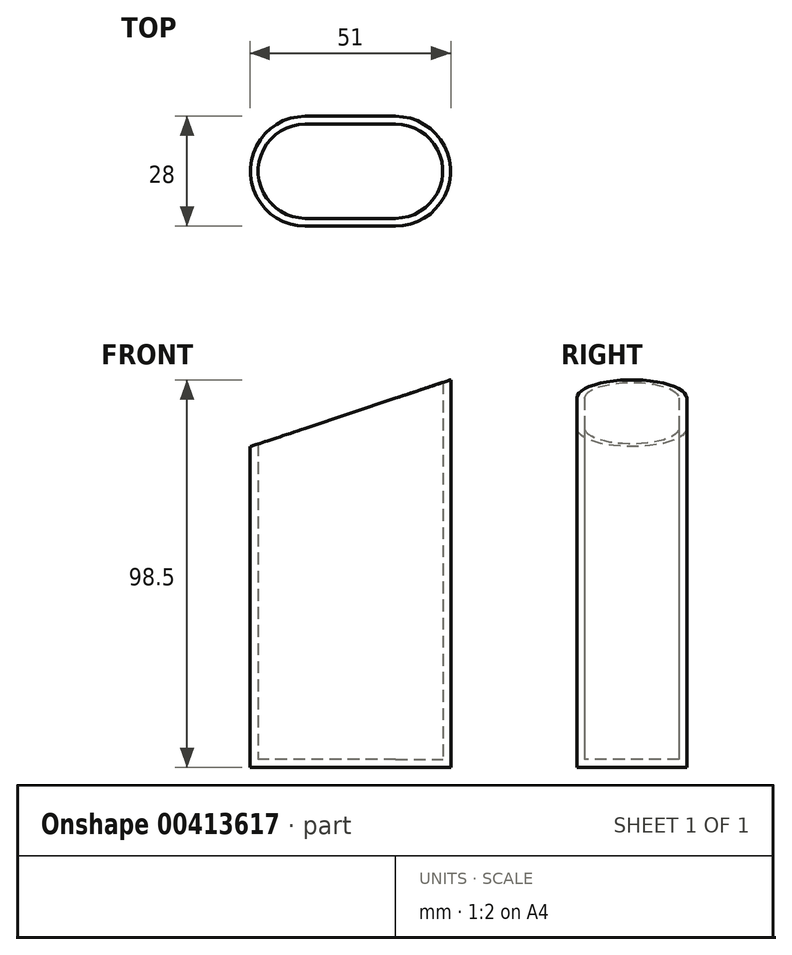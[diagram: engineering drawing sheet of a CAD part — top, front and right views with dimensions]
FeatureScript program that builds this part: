
annotation { "Feature Type Name" : "Feature", "Feature Type Description" : "" }
export const myFeature = defineFeature(function(context is Context, id is Id, definition is map)
    precondition{}
    {
        {
            var Q0;
            Q0=qCreatedBy(makeId("Top.planeOp"),FACE);
            var sketch = newSketch(context, id + "F0", { "sketchPlane" : qUnion([Q0])});
            skLineSegment(sketch, "E0.bottom", {"start": v(11.5, 12) * mm, "end": v(-11.5, 12) * mm});
            skLineSegment(sketch, "E0.top", {"start": v(11.5, -12) * mm, "end": v(-11.5, -12) * mm});
            skLineSegment(sketch, "E0.left", {"start": v(23.5, 0) * mm, "end": v(23.5, 0) * mm});
            skLineSegment(sketch, "E0.right", {"start": v(-23.5, 0) * mm, "end": v(-23.5, 0) * mm});
            skPoint(sketch, "E0.middle", {"position": v(0, 0) * mm});
            skPoint(sketch, "E1.visualSharp", {"position": v(23.5, 12) * mm});
            skArc(sketch, "E1.filletArc", {"start": v(23.5, 0) * mm, "mid": v(19.99, 8.49) * mm, "end": v(11.5, 12) * mm});
            skPoint(sketch, "E2.visualSharp", {"position": v(23.5, -12) * mm});
            skArc(sketch, "E2.filletArc", {"start": v(11.5, -12) * mm, "mid": v(19.99, -8.49) * mm, "end": v(23.5, 0) * mm});
            skPoint(sketch, "E3.visualSharp", {"position": v(-23.5, 12) * mm});
            skArc(sketch, "E3.filletArc", {"start": v(-11.5, 12) * mm, "mid": v(-19.99, 8.49) * mm, "end": v(-23.5, 0) * mm});
            skPoint(sketch, "E4.visualSharp", {"position": v(-23.5, -12) * mm});
            skArc(sketch, "E4.filletArc", {"start": v(-23.5, 0) * mm, "mid": v(-19.99, -8.49) * mm, "end": v(-11.5, -12) * mm});
            skArc(sketch, "E5.0", {"start": v(25.5, 0) * mm, "mid": v(21.4, 9.9) * mm, "end": v(11.5, 14) * mm});
            skArc(sketch, "E5.1", {"start": v(-11.5, 14) * mm, "mid": v(-21.4, -9.9) * mm, "end": v(2.5, 0) * mm});
            skArc(sketch, "E5.2", {"start": v(2.5, 0) * mm, "mid": v(-21.4, 9.9) * mm, "end": v(-11.5, -14) * mm});
            skLineSegment(sketch, "E5.3", {"start": v(11.5, 14) * mm, "end": v(-11.5, 14) * mm});
            skLineSegment(sketch, "E5.4", {"start": v(11.5, -14) * mm, "end": v(-11.5, -14) * mm});
            skArc(sketch, "E5.5", {"start": v(11.5, -14) * mm, "mid": v(21.4, -9.9) * mm, "end": v(25.5, 0) * mm});
            skPoint(sketch, "E6", {"position": v(2.5, 0) * mm});
            skPoint(sketch, "E7", {"position": v(25.5, 0) * mm});
            skSolve(sketch);
        }
        {
            var Q0;
            Q0=makeQuery(id+"F0.imprint","IMPRINT",FACE,{"disambiguationData":[TD([[makeQuery(id+"F0.imprint","IMPRINT",EDGE,{"derivedFrom":sQuery(id+"F0.wireOp",EDGE,"E0.bottom")}),1.0]])]});
            var Q1;
            Q1=makeQuery(id+"F0.imprint","IMPRINT",FACE,{"disambiguationData":[TD([[makeQuery(id+"F0.imprint","IMPRINT",EDGE,{"derivedFrom":sQuery(id+"F0.wireOp",EDGE,"E0.bottom")}),-1.0]])]});
            var Q2;
            {var subQ4=sQuery(id+"F0.wireOp",EDGE,"E3.filletArc");Q2=makeQuery(id+"F0.imprint","IMPRINT",FACE,{"disambiguationData":[TD([[makeQuery(id+"F0.imprint","IMPRINT",EDGE,{"derivedFrom":subQ4}),-1.0]])]});}
            extrude(context, id + "F1", {"entities" : qUnion([Q0, Q1, Q2]), "depth" : 2 * mm});
        }
        {
            var Q0;
            Q0 = qSketchRegion(id + "F0", true);
            extrude(context, id + "F2", {"entities" : qUnion([Q0]), "operationType" : NewBodyOperationType.ADD, "depth" : 100 * mm});
        }
        {
            var Q0;
            Q0=makeQuery(id+"F2.opExtrude","SWEPT_FACE",FACE,{"disambiguationData":[OSD([sQuery(id+"F0.wireOp",EDGE,"E5.3")])]});
            var sketch = newSketch(context, id + "F3", { "sketchPlane" : qUnion([Q0])});
            skLineSegment(sketch, "E8", {"start": v(-30, 100) * mm, "end": v(-30, 127.57) * mm});
            skLineSegment(sketch, "E9", {"start": v(-30, 127.57) * mm, "end": v(30, 127.57) * mm});
            skLineSegment(sketch, "E10", {"start": v(30, 127.57) * mm, "end": v(30, 80) * mm});
            skLineSegment(sketch, "E11", {"start": v(30, 80) * mm, "end": v(-30, 100) * mm});
            skSolve(sketch);
        }
        {
            var Q0;
            Q0 = qSketchRegion(id + "F3", true);
            extrude(context, id + "F4", {"entities" : qUnion([Q0]), "operationType" : NewBodyOperationType.REMOVE, "endBound" : BoundingType.THROUGH_ALL, "oppositeDirection" : true, "depth" : 25 * mm});
        }
    });
